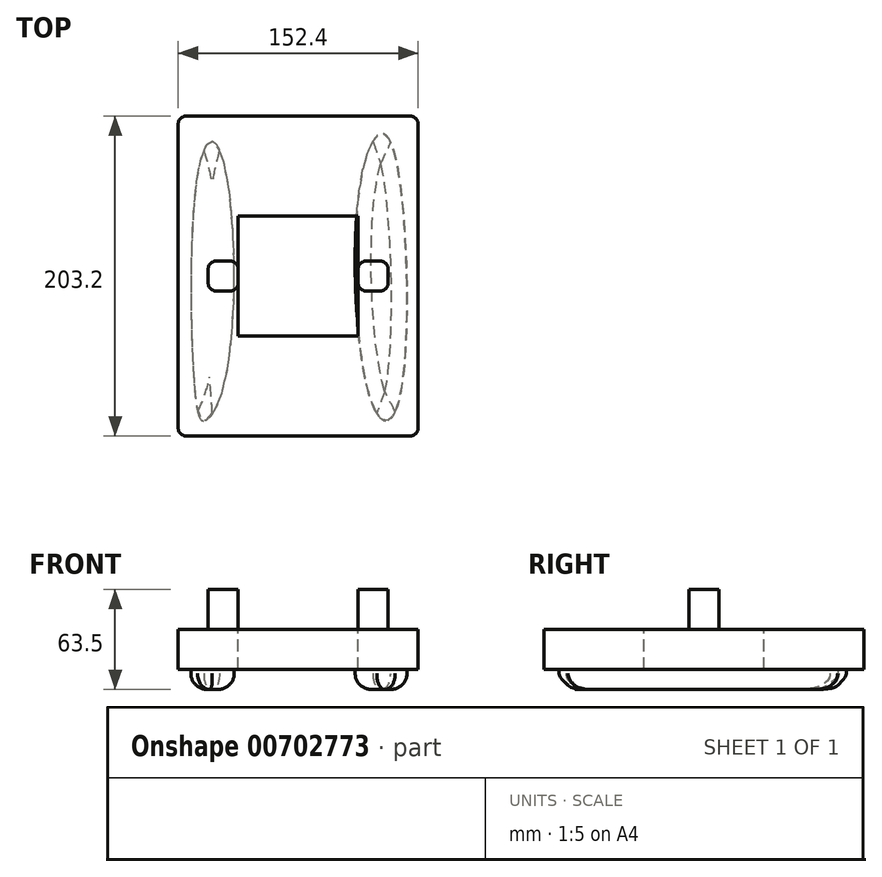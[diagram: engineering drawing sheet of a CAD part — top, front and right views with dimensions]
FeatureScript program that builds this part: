
annotation { "Feature Type Name" : "Feature", "Feature Type Description" : "" }
export const myFeature = defineFeature(function(context is Context, id is Id, definition is map)
    precondition{}
    {
        {
            var Q0;
            Q0=qCreatedBy(makeId("Top.planeOp"),FACE);
            var sketch = newSketch(context, id + "F0", { "sketchPlane" : qUnion([Q0])});
            skLineSegment(sketch, "E0.bottom", {"start": v(-152.4, 91.7) * mm, "end": v(0, 91.7) * mm});
            skLineSegment(sketch, "E0.top", {"start": v(-152.4, -111.5) * mm, "end": v(0, -111.5) * mm});
            skLineSegment(sketch, "E0.left", {"start": v(-152.4, 91.7) * mm, "end": v(-152.4, -111.5) * mm});
            skLineSegment(sketch, "E0.right", {"start": v(0, 91.7) * mm, "end": v(0, -111.5) * mm});
            skSolve(sketch);
        }
        {
            var Q0;
            Q0=qSketchRegion(id+"F0",true);
            extrude(context, id + "F1", {"entities" : qUnion([Q0]), "depth" : 25.4 * mm, "offsetDistance" : 25.4 * mm});
        }
        {
            var Q0;
            Q0=makeQuery(id+"F1.opExtrude","CAP_FACE",FACE,{"disambiguationData":[OSD([sQuery(id+"F0.wireOp",EDGE,"E0.bottom"),sQuery(id+"F0.wireOp",EDGE,"E0.top"),sQuery(id+"F0.wireOp",EDGE,"E0.left"),sQuery(id+"F0.wireOp",EDGE,"E0.right")])],"isStart":false});
            var sketch = newSketch(context, id + "F2", { "sketchPlane" : qUnion([Q0])});
            skLineSegment(sketch, "E1.bottom", {"start": v(-114.3, 28.2) * mm, "end": v(-38.1, 28.2) * mm});
            skLineSegment(sketch, "E1.top", {"start": v(-114.3, -48) * mm, "end": v(-38.1, -48) * mm});
            skLineSegment(sketch, "E1.left", {"start": v(-114.3, 28.2) * mm, "end": v(-114.3, -48) * mm});
            skLineSegment(sketch, "E1.right", {"start": v(-38.1, 28.2) * mm, "end": v(-38.1, -48) * mm});
            skSolve(sketch);
        }
        {
            var Q0;
            Q0=qSketchRegion(id+"F2",true);
            extrude(context, id + "F3", {"entities" : qUnion([Q0]), "operationType" : NewBodyOperationType.REMOVE, "oppositeDirection" : true, "depth" : 76.2 * mm, "offsetDistance" : 25.4 * mm});
        }
        {
            var Q0;
            Q0=makeQuery(id+"F1.opExtrude","CAP_FACE",FACE,{"disambiguationData":[OSD([sQuery(id+"F0.wireOp",EDGE,"E0.bottom"),sQuery(id+"F0.wireOp",EDGE,"E0.top"),sQuery(id+"F0.wireOp",EDGE,"E0.left"),sQuery(id+"F0.wireOp",EDGE,"E0.right")])],"isStart":false});
            var sketch = newSketch(context, id + "F4", { "sketchPlane" : qUnion([Q0])});
            skLineSegment(sketch, "E2.bottom", {"start": v(-114.3, -0.38) * mm, "end": v(-133.35, -0.38) * mm});
            skLineSegment(sketch, "E2.top", {"start": v(-114.3, -19.43) * mm, "end": v(-133.35, -19.43) * mm});
            skLineSegment(sketch, "E2.left", {"start": v(-114.3, -0.38) * mm, "end": v(-114.3, -19.43) * mm});
            skLineSegment(sketch, "E2.right", {"start": v(-133.35, -0.38) * mm, "end": v(-133.35, -19.43) * mm});
            skLineSegment(sketch, "E3.bottom", {"start": v(-38.1, -0.38) * mm, "end": v(-19.05, -0.38) * mm});
            skLineSegment(sketch, "E3.top", {"start": v(-38.1, -19.43) * mm, "end": v(-19.05, -19.43) * mm});
            skLineSegment(sketch, "E3.left", {"start": v(-38.1, -0.38) * mm, "end": v(-38.1, -19.43) * mm});
            skLineSegment(sketch, "E3.right", {"start": v(-19.05, -0.38) * mm, "end": v(-19.05, -19.43) * mm});
            skSolve(sketch);
        }
        {
            var Q0;
            Q0=qSketchRegion(id+"F4",true);
            extrude(context, id + "F5", {"entities" : qUnion([Q0]), "operationType" : NewBodyOperationType.ADD, "depth" : 25.4 * mm, "offsetDistance" : 25.4 * mm});
        }
        {
            var Q0;
            Q0=makeQuery(id+"F1.opExtrude","SWEPT_EDGE",EDGE,{"disambiguationData":[OSD([sQuery(id+"F0.wireOp",EDGE,"E0.bottom"),sQuery(id+"F0.wireOp",EDGE,"E0.right")])]});
            var Q1;
            Q1=makeQuery(id+"F1.opExtrude","SWEPT_EDGE",EDGE,{"disambiguationData":[OSD([sQuery(id+"F0.wireOp",EDGE,"E0.bottom"),sQuery(id+"F0.wireOp",EDGE,"E0.left")])]});
            fillet(context, id + "F6", {"entities" : qUnion([Q0, Q1]), "radius" : 5.08 * mm, "tangentPropagation" : true, "allowEdgeOverflow" : false});
        }
        {
            var Q0;
            Q0=makeQuery(id+"F1.opExtrude","SWEPT_EDGE",EDGE,{"disambiguationData":[OSD([sQuery(id+"F0.wireOp",EDGE,"E0.top"),sQuery(id+"F0.wireOp",EDGE,"E0.right")])]});
            var Q1;
            Q1=makeQuery(id+"F1.opExtrude","SWEPT_EDGE",EDGE,{"disambiguationData":[OSD([sQuery(id+"F0.wireOp",EDGE,"E0.top"),sQuery(id+"F0.wireOp",EDGE,"E0.left")])]});
            fillet(context, id + "F7", {"entities" : qUnion([Q0, Q1]), "radius" : 5.08 * mm, "tangentPropagation" : true, "allowEdgeOverflow" : false});
        }
        {
            var Q0;
            Q0=makeQuery(id+"F5.opExtrude","SWEPT_EDGE",EDGE,{"disambiguationData":[OSD([sQuery(id+"F2.wireOp",EDGE,"E1.left"),sQuery(id+"F4.wireOp",EDGE,"E2.bottom"),sQuery(id+"F4.wireOp",EDGE,"E2.left")])]});
            var Q1;
            Q1=makeQuery(id+"F5.opExtrude","SWEPT_EDGE",EDGE,{"disambiguationData":[OSD([sQuery(id+"F2.wireOp",EDGE,"E1.left"),sQuery(id+"F4.wireOp",EDGE,"E2.top"),sQuery(id+"F4.wireOp",EDGE,"E2.left")])]});
            var Q2;
            Q2=makeQuery(id+"F5.opExtrude","SWEPT_EDGE",EDGE,{"disambiguationData":[OSD([sQuery(id+"F4.wireOp",EDGE,"E3.bottom"),sQuery(id+"F4.wireOp",EDGE,"E3.right")])]});
            var Q3;
            Q3=makeQuery(id+"F5.opExtrude","SWEPT_EDGE",EDGE,{"disambiguationData":[OSD([sQuery(id+"F4.wireOp",EDGE,"E3.top"),sQuery(id+"F4.wireOp",EDGE,"E3.right")])]});
            var Q4;
            Q4=makeQuery(id+"F5.opExtrude","SWEPT_EDGE",EDGE,{"disambiguationData":[OSD([sQuery(id+"F2.wireOp",EDGE,"E1.right"),sQuery(id+"F4.wireOp",EDGE,"E3.bottom"),sQuery(id+"F4.wireOp",EDGE,"E3.left")])]});
            var Q5;
            Q5=makeQuery(id+"F5.opExtrude","SWEPT_EDGE",EDGE,{"disambiguationData":[OSD([sQuery(id+"F2.wireOp",EDGE,"E1.right"),sQuery(id+"F4.wireOp",EDGE,"E3.top"),sQuery(id+"F4.wireOp",EDGE,"E3.left")])]});
            var Q6;
            Q6=makeQuery(id+"F5.opExtrude","SWEPT_EDGE",EDGE,{"disambiguationData":[OSD([sQuery(id+"F4.wireOp",EDGE,"E2.bottom"),sQuery(id+"F4.wireOp",EDGE,"E2.right")])]});
            var Q7;
            Q7=makeQuery(id+"F5.opExtrude","SWEPT_EDGE",EDGE,{"disambiguationData":[OSD([sQuery(id+"F4.wireOp",EDGE,"E2.top"),sQuery(id+"F4.wireOp",EDGE,"E2.right")])]});
            fillet(context, id + "F8", {"entities" : qUnion([Q0, Q1, Q2, Q3, Q4, Q5, Q6, Q7]), "radius" : 5.08 * mm, "tangentPropagation" : true, "allowEdgeOverflow" : false});
        }
        {
            var Q0;
            Q0=makeQuery(id+"F1.opExtrude","CAP_FACE",FACE,{"disambiguationData":[OSD([sQuery(id+"F0.wireOp",EDGE,"E0.bottom"),sQuery(id+"F0.wireOp",EDGE,"E0.top"),sQuery(id+"F0.wireOp",EDGE,"E0.left"),sQuery(id+"F0.wireOp",EDGE,"E0.right")])],"isStart":true});
            var sketch = newSketch(context, id + "F9", { "sketchPlane" : qUnion([Q0])});
            skFitSpline(sketch, "E4", {"points": [v(-142.11, 80.7) * mm, v(-136.3, 101.99) * mm, v(-123.4, 80.05) * mm, v(-121.46, -53.55) * mm, v(-131.14, -75.49) * mm, v(-140.18, -54.84) * mm, v(-142.11, 80.7) * mm]});
            skFitSpline(sketch, "E5", {"points": [v(-20.14, 101.99) * mm, v(-32.4, 80.7) * mm, v(-35.63, -55.48) * mm, v(-22.72, -80.65) * mm, v(-12.4, -55.48) * mm, v(-10.46, 80.7) * mm, v(-20.14, 101.99) * mm]});
            skSolve(sketch);
        }
        {
            var Q0;
            Q0 = qSketchRegion(id + "F9", true);
            extrude(context, id + "F10", {"entities" : qUnion([Q0]), "operationType" : NewBodyOperationType.ADD, "depth" : 12.7 * mm, "offsetDistance" : 25.4 * mm});
        }
        {
            var Q0;
            Q0=makeQuery(id+"F10.opExtrude","CAP_FACE",FACE,{"disambiguationData":[OSD([sQuery(id+"F9.wireOp",EDGE,"E4")])],"isStart":false});
            var Q1;
            Q1=makeQuery(id+"F10.opExtrude","CAP_FACE",FACE,{"disambiguationData":[OSD([sQuery(id+"F9.wireOp",EDGE,"E5")])],"isStart":false});
            fillet(context, id + "F11", {"entities" : qUnion([Q0, Q1]), "radius" : 10.16 * mm, "tangentPropagation" : true, "allowEdgeOverflow" : false});
        }
    });
